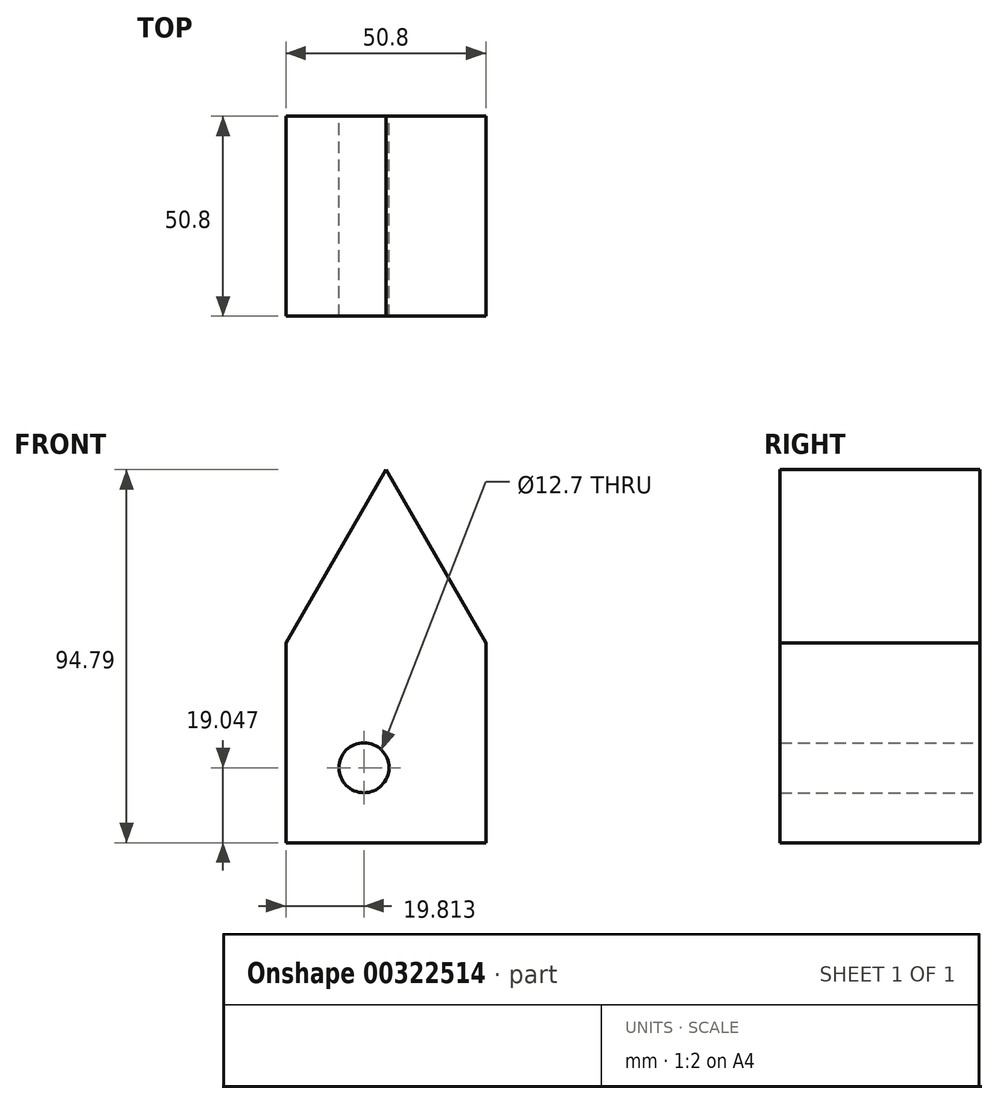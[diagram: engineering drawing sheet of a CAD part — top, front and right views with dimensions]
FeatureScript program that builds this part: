
annotation { "Feature Type Name" : "Feature", "Feature Type Description" : "" }
export const myFeature = defineFeature(function(context is Context, id is Id, definition is map)
    precondition{}
    {
        {
            var Q0;
            Q0=qCreatedBy(makeId("Front.planeOp"),FACE);
            var sketch = newSketch(context, id + "F0", { "sketchPlane" : qUnion([Q0])});
            skLineSegment(sketch, "E0.top", {"start": v(-25.32, -27.7) * mm, "end": v(25.48, -27.7) * mm});
            skLineSegment(sketch, "E0.left", {"start": v(-25.32, 23.1) * mm, "end": v(-25.32, -27.7) * mm});
            skLineSegment(sketch, "E0.right", {"start": v(25.48, 23.1) * mm, "end": v(25.48, -27.7) * mm});
            skLineSegment(sketch, "E1", {"start": v(-25.32, 23.1) * mm, "end": v(0.08, 67.1) * mm});
            skLineSegment(sketch, "E2", {"start": v(0.08, 67.1) * mm, "end": v(25.48, 23.1) * mm});
            skLineSegment(sketch, "E3.0", {"start": v(-24.56, -8.64) * mm, "end": v(-5.5, -8.64) * mm});
            skLineSegment(sketch, "E4.trimOffspring", {"start": v(-5.5, -8.64) * mm, "end": v(-5.5, -28.15) * mm});
            skCircle(sketch, "E5", {"center": v(-5.5, -8.64) * mm, "radius": 6.35 * mm});
            skSolve(sketch);
        }
        {
            var Q0;
            {var subQ1=sQuery(id+"F0.wireOp",EDGE,"E0.left");Q0=makeQuery(id+"F0.imprint","IMPRINT",FACE,{"disambiguationData":[TD([[makeQuery(id+"F0.imprint","IMPRINT",EDGE,{"derivedFrom":subQ1}),1.0]])]});}
            extrude(context, id + "F1", {"entities" : qUnion([Q0]), "depth" : 50.8 * mm});
        }
    });
